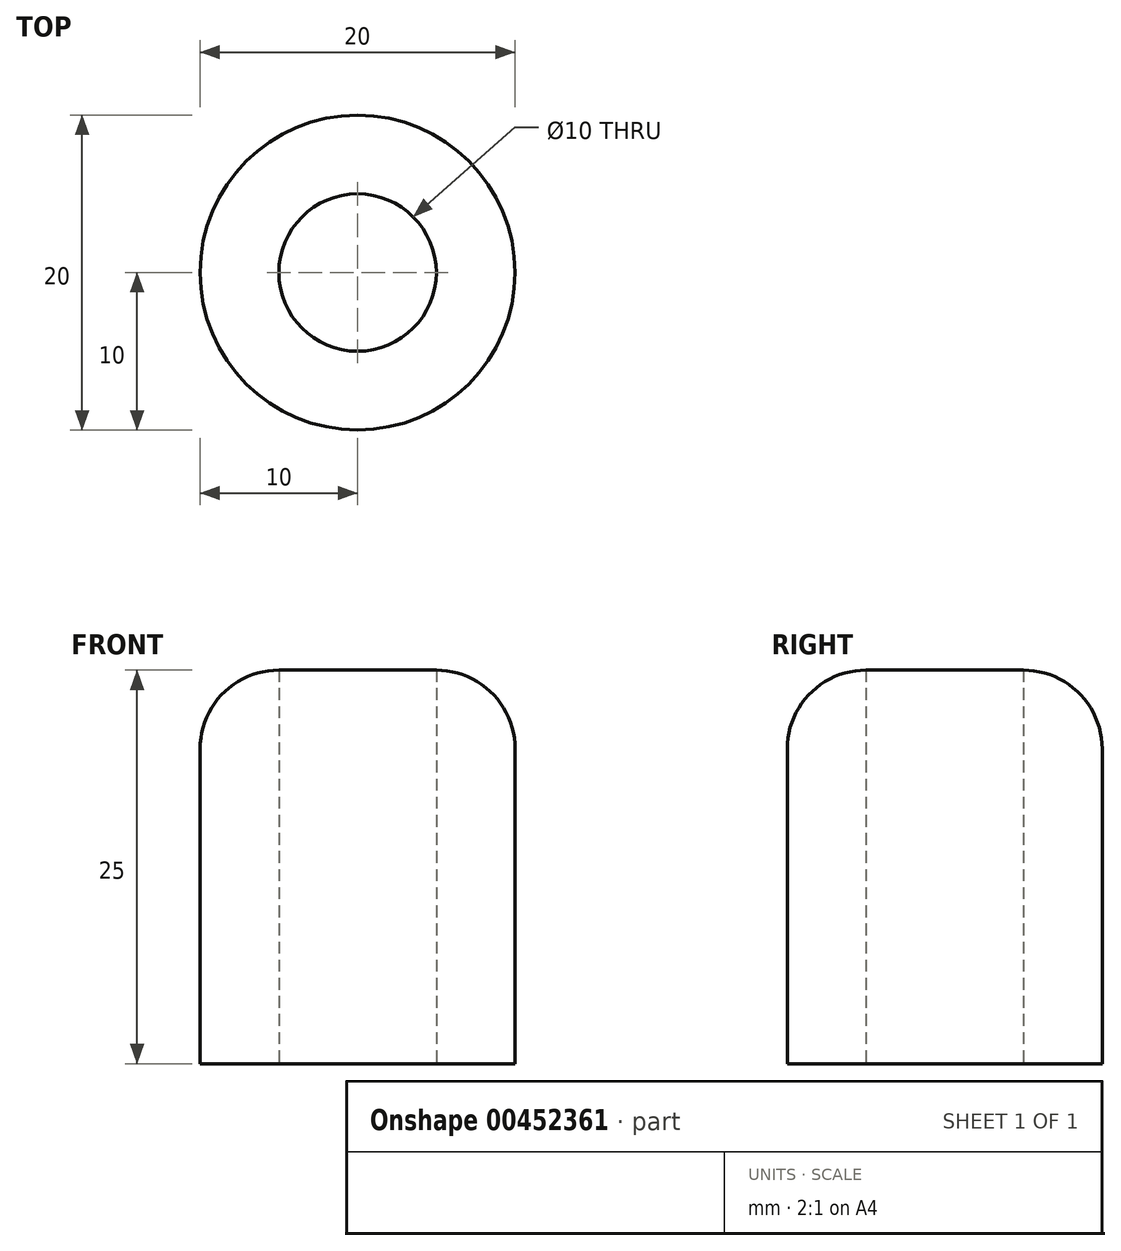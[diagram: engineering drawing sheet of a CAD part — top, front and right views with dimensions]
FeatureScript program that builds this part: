
annotation { "Feature Type Name" : "Feature", "Feature Type Description" : "" }
export const myFeature = defineFeature(function(context is Context, id is Id, definition is map)
    precondition{}
    {
        {
            var Q0;
            Q0=qCreatedBy(makeId("Top.planeOp"),FACE);
            var sketch = newSketch(context, id + "F0", { "sketchPlane" : qUnion([Q0])});
            skCircle(sketch, "E0", {"center": v(0, 0) * mm, "radius": 10 * mm});
            skCircle(sketch, "E1", {"center": v(0, 0) * mm, "radius": 5 * mm});
            skSolve(sketch);
        }
        {
            var Q0;
            Q0 = qSketchRegion(id + "F0", true);
            extrude(context, id + "F1", {"entities" : qUnion([Q0]), "depth" : 25 * mm});
        }
        {
            var Q0;
            Q0 = qSketchRegion(id + "F0", true);
            extrude(context, id + "F2", {"entities" : qUnion([Q0]), "operationType" : NewBodyOperationType.ADD, "depth" : 25 * mm});
        }
        {
            var Q0;
            Q0=makeQuery(id+"F1.opExtrude","CAP_EDGE",EDGE,{"disambiguationData":[OSD([sQuery(id+"F0.wireOp",EDGE,"E0")])],"isStart":false});
            fillet(context, id + "F3", {"entities" : qUnion([Q0]), "radius" : 5 * mm, "tangentPropagation" : true, "allowEdgeOverflow" : false});
        }
    });
